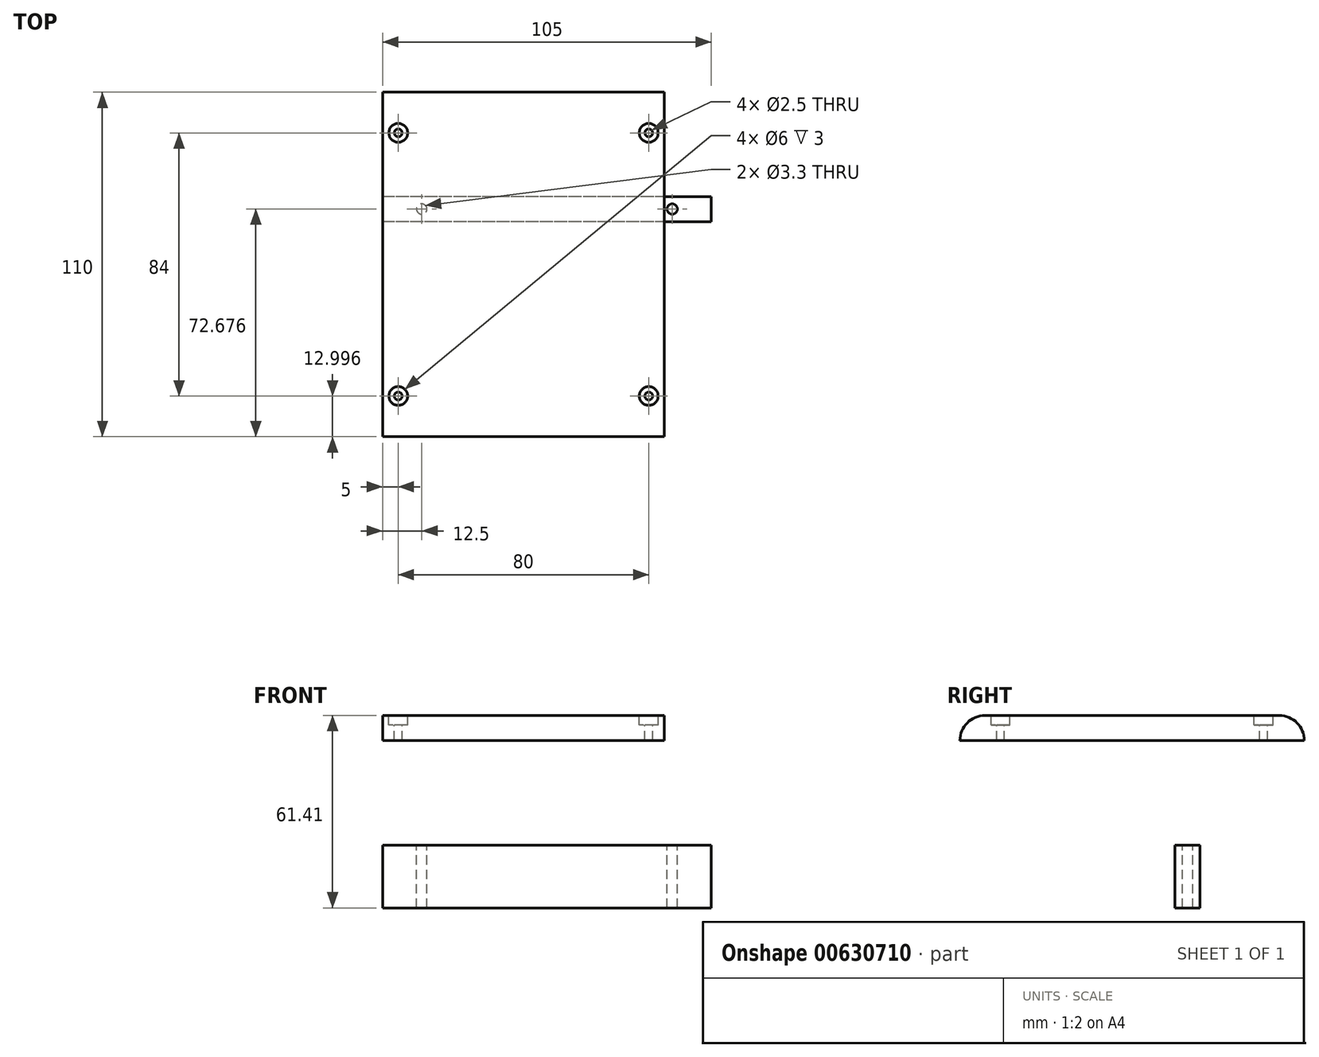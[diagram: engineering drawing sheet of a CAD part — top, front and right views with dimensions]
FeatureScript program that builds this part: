
annotation { "Feature Type Name" : "Feature", "Feature Type Description" : "" }
export const myFeature = defineFeature(function(context is Context, id is Id, definition is map)
    precondition{}
    {
        {
            var Q0;
            Q0=qCreatedBy(makeId("Right.planeOp"),FACE);
            var sketch = newSketch(context, id + "F0", { "sketchPlane" : qUnion([Q0])});
            skLineSegment(sketch, "E0.bottom", {"start": v(-32.7, 24.8) * mm, "end": v(61.3, 24.8) * mm});
            skLineSegment(sketch, "E0.top", {"start": v(-40.7, 16.8) * mm, "end": v(69.3, 16.8) * mm});
            skLineSegment(sketch, "E0.left", {"start": v(-40.7, 16.8) * mm, "end": v(-40.7, 16.8) * mm});
            skLineSegment(sketch, "E0.right", {"start": v(69.3, 16.8) * mm, "end": v(69.3, 16.8) * mm});
            skPoint(sketch, "E1.visualSharp", {"position": v(69.3, 24.8) * mm});
            skArc(sketch, "E1.filletArc", {"start": v(69.3, 16.8) * mm, "mid": v(66.95, 22.46) * mm, "end": v(61.3, 24.8) * mm});
            skPoint(sketch, "E2.visualSharp", {"position": v(-40.7, 24.8) * mm});
            skArc(sketch, "E2.filletArc", {"start": v(-32.7, 24.8) * mm, "mid": v(-38.36, 22.46) * mm, "end": v(-40.7, 16.8) * mm});
            skSolve(sketch);
        }
        {
            var Q0;
            Q0=makeQuery(id+"F0.imprint","IMPRINT",FACE,{"disambiguationData":[TD([[makeQuery(id+"F0.imprint","IMPRINT",EDGE,{"derivedFrom":sQuery(id+"F0.wireOp",EDGE,"E0.bottom")}),-1.0]])]});
            extrude(context, id + "F1", {"entities" : qUnion([Q0]), "depth" : 90 * mm, "offsetDistance" : 25 * mm});
        }
        {
            var Q0;
            Q0=makeQuery(id+"F1.opExtrude","SWEPT_FACE",FACE,{"disambiguationData":[OSD([sQuery(id+"F0.wireOp",EDGE,"E0.bottom")])]});
            var sketch = newSketch(context, id + "F2", { "sketchPlane" : qUnion([Q0])});
            skPoint(sketch, "E3", {"position": v(5, 56.3) * mm});
            skLineSegment(sketch, "E4", {"start": v(45, 61.3) * mm, "end": v(45, -32.7) * mm, "construction": true});
            skLineSegment(sketch, "E5", {"start": v(0, 14.3) * mm, "end": v(90, 14.3) * mm, "construction": true});
            skPoint(sketch, "E6.MirrorP", {"position": v(5, -27.7) * mm});
            skPoint(sketch, "E7.MirrorP", {"position": v(85, 56.3) * mm});
            skPoint(sketch, "E8.MirrorP", {"position": v(85, -27.7) * mm});
            skSolve(sketch);
        }
        {
            var Q0;
            Q0=sQuery(id+"F2.wireOp",VERTEX,"E3");
            var Q1;
            Q1=sQuery(id+"F2.wireOp",VERTEX,"E7.MirrorP");
            var Q2;
            Q2=sQuery(id+"F2.wireOp",VERTEX,"E8.MirrorP");
            var Q3;
            Q3=sQuery(id+"F2.wireOp",VERTEX,"E6.MirrorP");
            var Q4;
            Q4=makeQuery(id+"F1.opExtrude","SWEPT_BODY",BODY,{"disambiguationData":[OSD([sQuery(id+"F0.wireOp",EDGE,"E0.bottom"),sQuery(id+"F0.wireOp",EDGE,"E0.top"),sQuery(id+"F0.wireOp",EDGE,"E1.filletArc"),sQuery(id+"F0.wireOp",EDGE,"E2.filletArc")])]});
            hole(context, id + "F3", {"style" : HoleStyle.C_BORE, "endStyle" : HoleEndStyle.THROUGH, "holeDiameter" : 2.5 * mm, "cBoreDiameter" : 6 * mm, "cBoreDepth" : 3 * mm, "majorDiameter" : 3 * mm, "isTappedThrough" : true, "tappedDepth" : 12 * mm, "tapClearance" : 3, "locations" : qUnion([Q0, Q1, Q2, Q3]), "scope" : qUnion([Q4])});
        }
        {
            var Q0;
            Q0=qCreatedBy(makeId("Right.planeOp"),FACE);
            var sketch = newSketch(context, id + "F4", { "sketchPlane" : qUnion([Q0])});
            skLineSegment(sketch, "E9.bottom", {"start": v(27.98, -16.6) * mm, "end": v(35.98, -16.6) * mm});
            skLineSegment(sketch, "E9.top", {"start": v(27.98, -36.6) * mm, "end": v(35.98, -36.6) * mm});
            skLineSegment(sketch, "E9.left", {"start": v(27.98, -16.6) * mm, "end": v(27.98, -36.6) * mm});
            skLineSegment(sketch, "E9.right", {"start": v(35.98, -16.6) * mm, "end": v(35.98, -36.6) * mm});
            skSolve(sketch);
        }
        {
            var Q0;
            Q0 = qSketchRegion(id + "F4", true);
            extrude(context, id + "F5", {"entities" : qUnion([Q0]), "depth" : 105 * mm, "offsetDistance" : 25 * mm});
        }
        {
            var Q0;
            Q0=makeQuery(id+"F5.opExtrude","SWEPT_FACE",FACE,{"disambiguationData":[OSD([sQuery(id+"F4.wireOp",EDGE,"E9.bottom")])]});
            var sketch = newSketch(context, id + "F6", { "sketchPlane" : qUnion([Q0])});
            skLineSegment(sketch, "E10", {"start": v(52.5, 35.98) * mm, "end": v(52.5, 27.98) * mm, "construction": true});
            skLineSegment(sketch, "E11", {"start": v(12.5, 35.98) * mm, "end": v(12.5, 27.98) * mm, "construction": true});
            skPoint(sketch, "E12", {"position": v(12.5, 31.98) * mm});
            skPoint(sketch, "E13.MirrorP", {"position": v(92.5, 31.98) * mm});
            skSolve(sketch);
        }
        {
            var Q0;
            Q0=sQuery(id+"F6.wireOp",VERTEX,"E12");
            var Q1;
            Q1=sQuery(id+"F6.wireOp",VERTEX,"E13.MirrorP");
            var Q2;
            Q2=makeQuery(id+"F5.opExtrude","SWEPT_BODY",BODY,{"disambiguationData":[OSD([sQuery(id+"F4.wireOp",EDGE,"E9.bottom"),sQuery(id+"F4.wireOp",EDGE,"E9.top"),sQuery(id+"F4.wireOp",EDGE,"E9.left"),sQuery(id+"F4.wireOp",EDGE,"E9.right")])]});
            hole(context, id + "F7", {"style" : HoleStyle.SIMPLE, "endStyle" : HoleEndStyle.THROUGH, "standardTappedOrClearance" : lookupTablePath({ "standard" : "ISO", "fit" : "Normal", "size" : "M3", "type" : "Clearance" }), "standardBlindInLast" : lookupTablePath({ "fit" : "Standard", "standard" : "ISO", "size" : "M3", "type" : "Clearance" }), "holeDiameter" : 3.3 * mm, "majorDiameter" : 5 * mm, "isTappedThrough" : true, "tappedDepth" : 12 * mm, "tapClearance" : 3, "locations" : qUnion([Q0, Q1]), "scope" : qUnion([Q2])});
        }
    });
